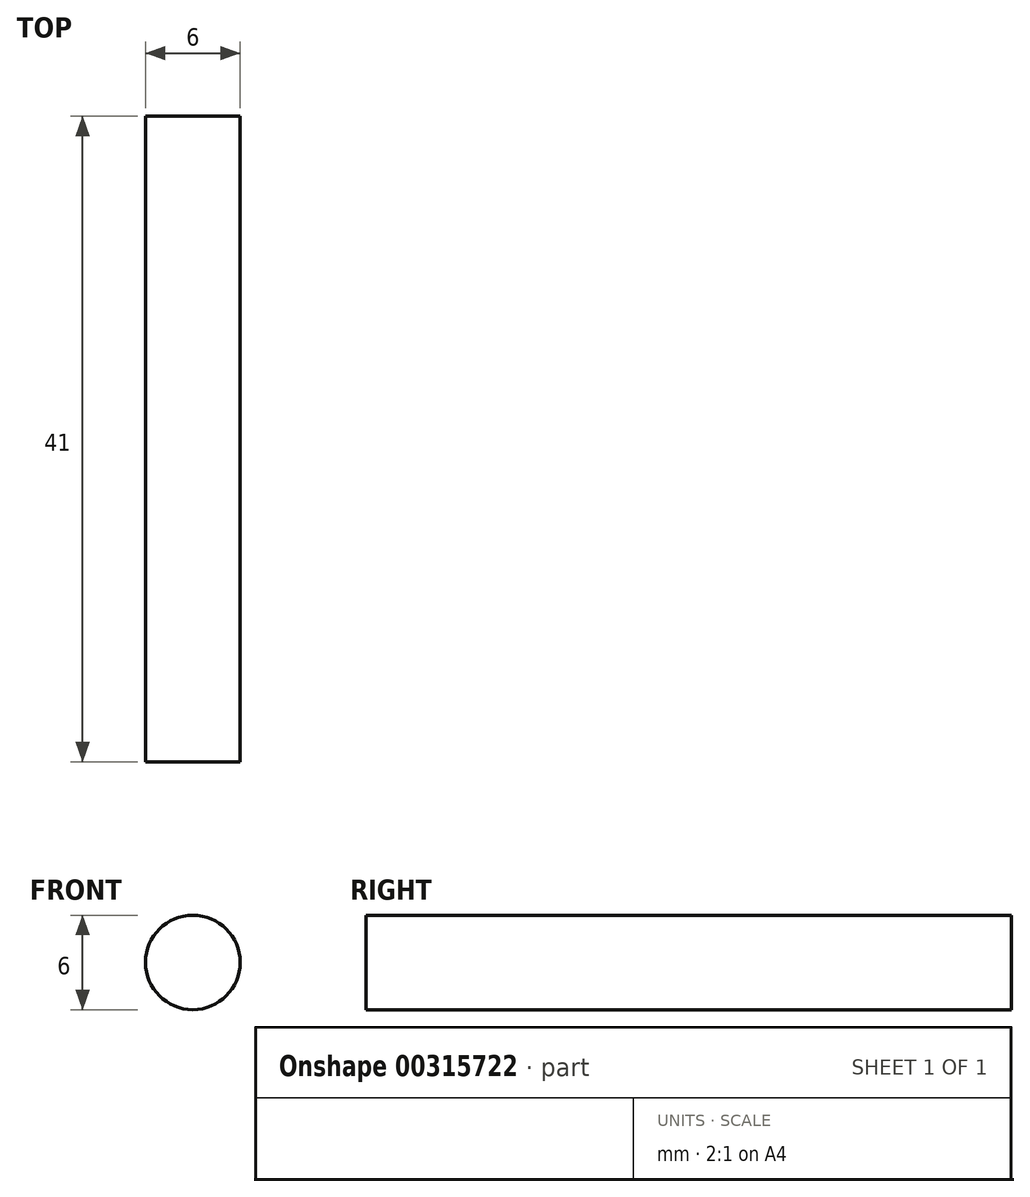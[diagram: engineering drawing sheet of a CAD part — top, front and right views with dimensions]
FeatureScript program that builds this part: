
annotation { "Feature Type Name" : "Feature", "Feature Type Description" : "" }
export const myFeature = defineFeature(function(context is Context, id is Id, definition is map)
    precondition{}
    {
        {
            var Q0;
            Q0=qCreatedBy(makeId("Front.planeOp"),FACE);
            var sketch = newSketch(context, id + "F0", { "sketchPlane" : qUnion([Q0])});
            skCircle(sketch, "E0", {"center": v(0, 0) * mm, "radius": 3 * mm});
            skSolve(sketch);
        }
        {
            var Q0;
            Q0=makeQuery(id+"F0.imprint","IMPRINT",FACE,{"disambiguationData":[TD([[makeQuery(id+"F0.imprint","IMPRINT",EDGE,{"derivedFrom":sQuery(id+"F0.wireOp",EDGE,"E0")}),1.0]])]});
            extrude(context, id + "F1", {"entities" : qUnion([Q0]), "depth" : 41 * mm});
        }
    });
